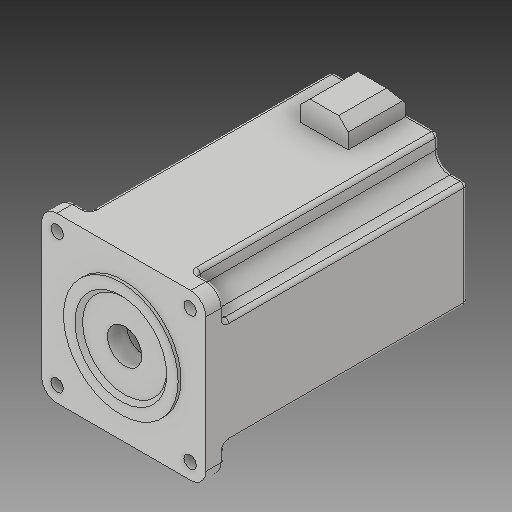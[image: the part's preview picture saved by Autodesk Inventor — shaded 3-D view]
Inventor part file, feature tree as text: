
AUTODESK INVENTOR PART (.ipt)
format: ipt  version: 2018 (Build 220112000, 112)  size: 385,536 bytes
history: native  units: mm
features: extrude x13, sketch x13, chamfer x5, projected_geometry x4, fillet x3, hole x1, plane x1
ambient origin geometry x8: Origin, YZ Plane, XZ Plane, XY Plane, X Axis, Y Axis, Z Axis, Center Point
bodies: Solid1 (feature_tree)
feature tree (40):
  extrude  "Extrusion1"  Depth=86.0mm
  extrude  "Extrusion2"  Depth=140.0mm
  extrude  "Extrusion3"  Depth=1.5mm
  hole  "Hole1"  [1 undecoded]
  plane  "Work Plane1"
  extrude  "Extrusion4"  Depth=13.0mm TaperAngle=0.0deg
  sketch  "Sketch6"  dims[d13=3.0mm d14=6.0mm d15=4.0mm d16=2.0mm d17=90.0deg d18=13.0mm d19=0.0mm d24=2.438mm d25=0.0mm]
  extrude  "Extrusion6"  Depth=69.6mm
  extrude  "Extrusion7"  Depth=120.0mm TaperAngle=0.0deg
  chamfer  "Chamfer1"  Distance=13.0mm
  fillet  "Fillet1"  Radius=8.0mm
  chamfer  "Chamfer2"  Distance=5.0mm Angle=45.0deg
  chamfer  "Chamfer3"  Distance=1.0mm Angle=45.0deg
  extrude  "Extrusion8"  Depth=56.0mm
  extrude  "Extrusion9"  Depth=3.0mm TaperAngle=45.0deg
  chamfer  "Chamfer4"  Distance=2.0mm
  fillet  "Fillet3"  Radius=15.0mm
  extrude  "Extrusion10"  Depth=15.0mm
  fillet  "Fillet4"  Radius=40.0mm
  extrude  "Extrusion11"  Depth=130.0mm TaperAngle=0.0deg
  chamfer  "Chamfer5"  Distance=2.0mm
  extrude  "Extrusion13"  Depth=8.0mm
  extrude  "Extrusion14"  Depth=2.0mm TaperAngle=0.0deg
  extrude  "Extrusion15"  Depth=2.0mm TaperAngle=45.0deg
  sketch  "Sketch1"  dims[d0=86.0mm d1=86.0mm]
  sketch  "Sketch2"  dims[d2=140.0mm d3=0.0mm d5=60.0mm]
  sketch  "Sketch3"  dims[d6=1.5mm d7=0.0mm d8=14.0mm]
  sketch  "Sketch5"  dims[d9=40.0mm d10=0.0mm d11=10.0mm d12=10.0mm]
  projected_geometry  "Projected Loop1"
  sketch  "Sketch7"  dims[d36=6.5mm d37=69.6mm]
  projected_geometry  "Projected Loop2"
  sketch  "Sketch8"  dims[d38=69.6mm d39=120.0mm d40=0.0mm]
  sketch  "Sketch9"  dims[d41=25.0mm]
  projected_geometry  "Projected Loop3"
  sketch  "Sketch10"  dims[d42=30.0mm]
  sketch  "Sketch11"  dims[d43=5.0mm d46=13.0mm d47=0.0mm]
  sketch  "Sketch13"  dims[d48=5.0mm d49=7.0mm d50=45.0deg d51=8.0mm d53=5.0mm d54=7.0mm d55=45.0deg d56=1.0mm d57=7.0mm d58=45.0deg]
  projected_geometry  "Projected Loop5"
  sketch  "Sketch14"  dims[d59=3.0mm d60=0.0mm d61=56.0mm]
  sketch  "Sketch15"  dims[d62=3.0mm d63=0.0mm d64=3.0mm d65=7.0mm d66=45.0deg d67=2.0mm d71=15.0mm d72=15.0mm d73=40.0mm d75=360.0deg d77=130.0mm d78=0.0mm d79=2.0mm d81=8.0mm d82=2.0mm d83=0.0mm d84=2.0mm d85=7.0mm d86=45.0deg d90=13.0mm d91=10.0mm d92=0.0mm d93=10.0mm d94=0.0mm d95=10.0mm d96=0.0mm]
note: 1 required parameter value undecoded (feature->parameter linkage not recoverable at this tier; creation-order binding heuristic only, values carry confidence <= 0.55)
